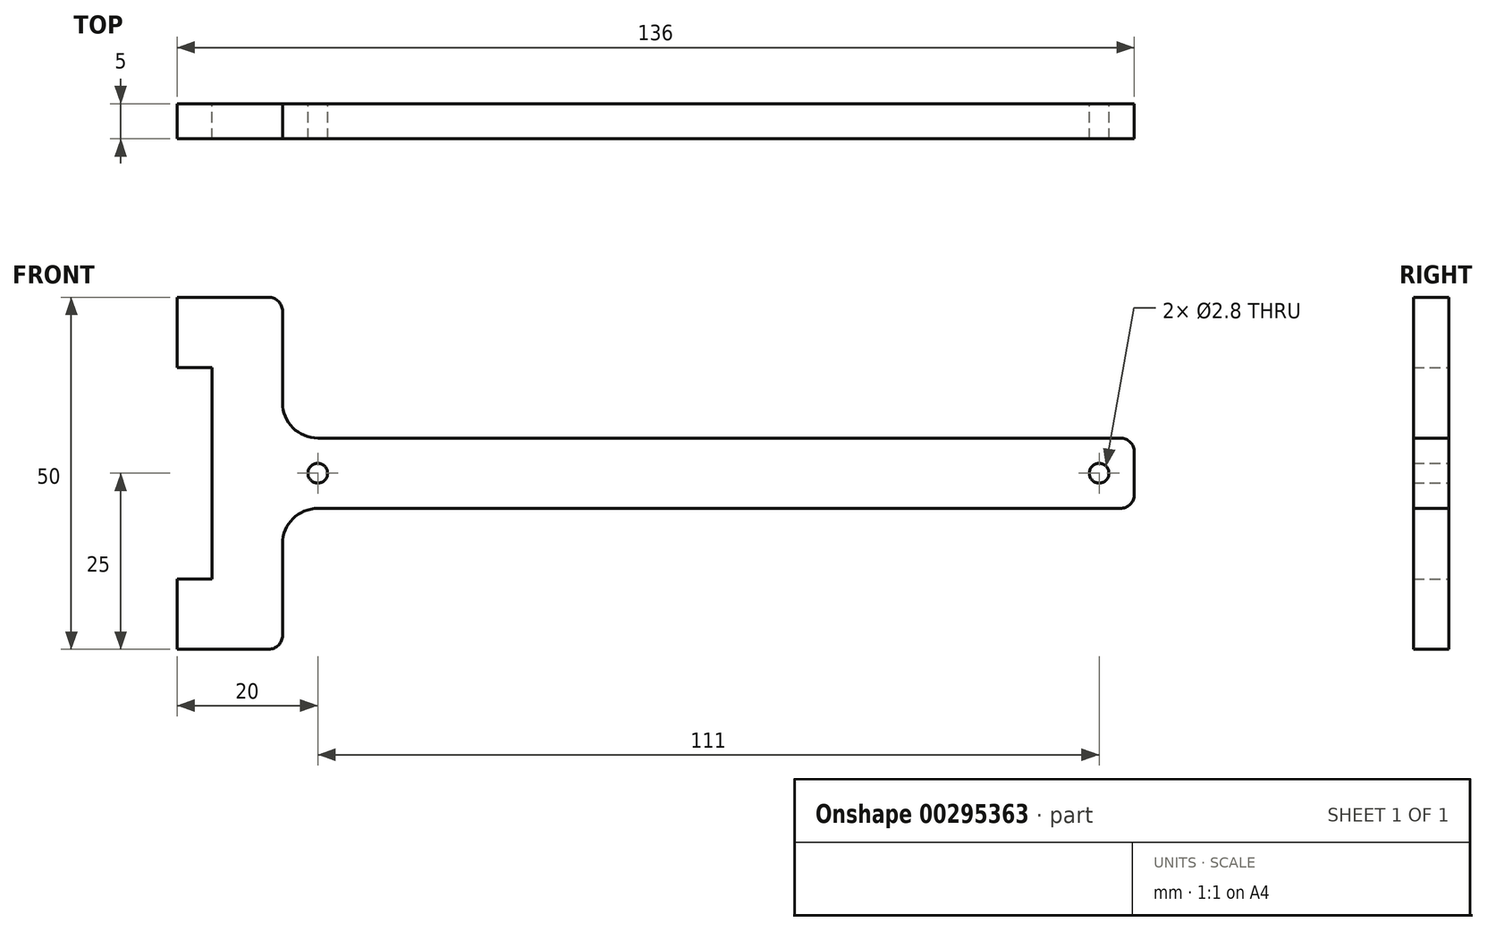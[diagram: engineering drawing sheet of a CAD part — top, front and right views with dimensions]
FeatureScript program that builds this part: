
annotation { "Feature Type Name" : "Feature", "Feature Type Description" : "" }
export const myFeature = defineFeature(function(context is Context, id is Id, definition is map)
    precondition{}
    {
        {
            var Q0;
            Q0=qCreatedBy(makeId("Front.planeOp"),FACE);
            var sketch = newSketch(context, id + "F0", { "sketchPlane" : qUnion([Q0])});
            skLineSegment(sketch, "E0.bottom", {"start": v(0, -5) * mm, "end": v(114, -5) * mm});
            skLineSegment(sketch, "E0.top", {"start": v(0, 5) * mm, "end": v(114, 5) * mm});
            skLineSegment(sketch, "E0.right", {"start": v(116, -3) * mm, "end": v(116, 3) * mm});
            skPoint(sketch, "E0.middle", {"position": v(50.5, 0) * mm});
            skCircle(sketch, "E1", {"center": v(0, 0) * mm, "radius": 1.4 * mm});
            skCircle(sketch, "E2", {"center": v(111, 0) * mm, "radius": 1.4 * mm});
            skLineSegment(sketch, "E3.bottom", {"start": v(-7, -25) * mm, "end": v(-15, -25) * mm});
            skLineSegment(sketch, "E3.top", {"start": v(-7, 25) * mm, "end": v(-15, 25) * mm});
            skLineSegment(sketch, "E3.left", {"start": v(-5, 10) * mm, "end": v(-5, 23) * mm});
            skLineSegment(sketch, "E3.right", {"start": v(-15, -15) * mm, "end": v(-15, 15) * mm});
            skPoint(sketch, "E3.middle", {"position": v(-10, 0) * mm});
            skArc(sketch, "E4.filletArc", {"start": v(-5, 10) * mm, "mid": v(-3.54, 6.46) * mm, "end": v(0, 5) * mm});
            skLineSegment(sketch, "E5", {"start": v(-5, -10) * mm, "end": v(-5, -23) * mm});
            skPoint(sketch, "E6.visualSharp", {"position": v(-5, -5) * mm});
            skArc(sketch, "E6.filletArc", {"start": v(0, -5) * mm, "mid": v(-3.54, -6.46) * mm, "end": v(-5, -10) * mm});
            skPoint(sketch, "E7.visualSharp", {"position": v(116, 5) * mm});
            skArc(sketch, "E7.filletArc", {"start": v(116, 3) * mm, "mid": v(115.41, 4.41) * mm, "end": v(114, 5) * mm});
            skPoint(sketch, "E8.visualSharp", {"position": v(116, -5) * mm});
            skArc(sketch, "E8.filletArc", {"start": v(114, -5) * mm, "mid": v(115.41, -4.41) * mm, "end": v(116, -3) * mm});
            skPoint(sketch, "E9.visualSharp", {"position": v(-5, 25) * mm});
            skArc(sketch, "E9.filletArc", {"start": v(-5, 23) * mm, "mid": v(-5.59, 24.41) * mm, "end": v(-7, 25) * mm});
            skPoint(sketch, "E10.visualSharp", {"position": v(-5, -25) * mm});
            skArc(sketch, "E10.filletArc", {"start": v(-7, -25) * mm, "mid": v(-5.59, -24.41) * mm, "end": v(-5, -23) * mm});
            skLineSegment(sketch, "E11.bottom", {"start": v(-15, 25) * mm, "end": v(-20, 25) * mm});
            skLineSegment(sketch, "E11.top", {"start": v(-15, 15) * mm, "end": v(-20, 15) * mm});
            skLineSegment(sketch, "E12.bottom", {"start": v(-15, -25) * mm, "end": v(-20, -25) * mm});
            skLineSegment(sketch, "E12.top", {"start": v(-15, -15) * mm, "end": v(-20, -15) * mm});
            skLineSegment(sketch, "E13.left", {"start": v(-20, -25) * mm, "end": v(-20, -15) * mm});
            skLineSegment(sketch, "E14.bottom", {"start": v(-28.54, -25) * mm, "end": v(-33.54, -25) * mm});
            skLineSegment(sketch, "E14.top", {"start": v(-28.54, 25) * mm, "end": v(-33.54, 25) * mm});
            skLineSegment(sketch, "E14.left", {"start": v(-28.54, -25) * mm, "end": v(-28.54, 25) * mm});
            skLineSegment(sketch, "E14.right", {"start": v(-33.54, -25) * mm, "end": v(-33.54, 25) * mm});
            skPoint(sketch, "E14.middle", {"position": v(-31.04, 0) * mm});
            skLineSegment(sketch, "E15", {"start": v(-28.54, -25) * mm, "end": v(-23.54, -25) * mm});
            skLineSegment(sketch, "E16", {"start": v(-23.54, -25) * mm, "end": v(-23.54, 25) * mm});
            skLineSegment(sketch, "E17", {"start": v(-23.54, 25) * mm, "end": v(-28.54, 25) * mm});
            skLineSegment(sketch, "E18.trimOffspring", {"start": v(-20, 15) * mm, "end": v(-20, 25) * mm});
            skSolve(sketch);
        }
        {
            var Q0;
            Q0=makeQuery(id+"F0.imprint","IMPRINT",FACE,{"disambiguationData":[TD([[makeQuery(id+"F0.imprint","IMPRINT",EDGE,{"derivedFrom":sQuery(id+"F0.wireOp",EDGE,"E0.bottom")}),1.0]])]});
            extrude(context, id + "F1", {"entities" : qUnion([Q0]), "depth" : 5 * mm});
        }
    });
